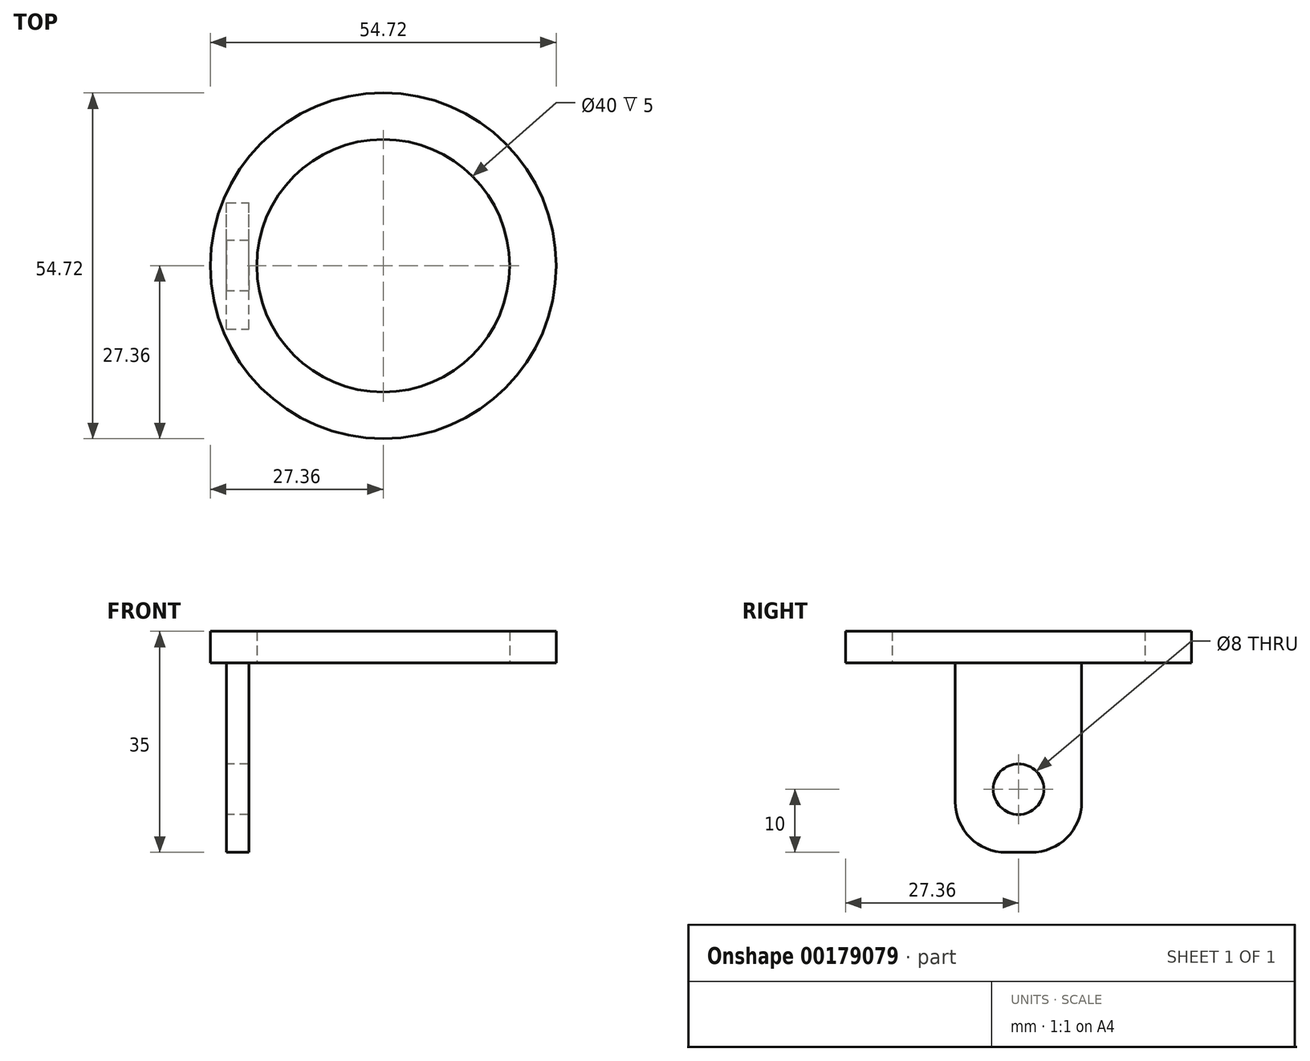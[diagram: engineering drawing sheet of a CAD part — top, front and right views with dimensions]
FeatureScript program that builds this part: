
annotation { "Feature Type Name" : "Feature", "Feature Type Description" : "" }
export const myFeature = defineFeature(function(context is Context, id is Id, definition is map)
    precondition{}
    {
        {
            var Q0;
            Q0=qCreatedBy(makeId("Top.planeOp"),FACE);
            var sketch = newSketch(context, id + "F0", { "sketchPlane" : qUnion([Q0])});
            skCircle(sketch, "E0", {"center": v(0, 0) * mm, "radius": 20 * mm});
            skCircle(sketch, "E1", {"center": v(0, 0) * mm, "radius": 27.36 * mm});
            skSolve(sketch);
        }
        {
            var Q0;
            Q0=makeQuery(id+"F0.imprint","IMPRINT",FACE,{"disambiguationData":[TD([[makeQuery(id+"F0.imprint","IMPRINT",EDGE,{"derivedFrom":sQuery(id+"F0.wireOp",EDGE,"E0")}),-1.0]])]});
            extrude(context, id + "F1", {"entities" : qUnion([Q0]), "depth" : 5 * mm});
        }
        {
            var Q0;
            Q0=makeQuery(id+"F1.opExtrude","CAP_FACE",FACE,{"disambiguationData":[OSD([sQuery(id+"F0.wireOp",EDGE,"E0"),sQuery(id+"F0.wireOp",EDGE,"E1")])],"isStart":true});
            var sketch = newSketch(context, id + "F2", { "sketchPlane" : qUnion([Q0])});
            skLineSegment(sketch, "E2.bottom", {"start": v(-24.79, 10) * mm, "end": v(-21.22, 10) * mm});
            skLineSegment(sketch, "E2.top", {"start": v(-24.79, -10) * mm, "end": v(-21.22, -10) * mm});
            skLineSegment(sketch, "E2.left", {"start": v(-24.79, 10) * mm, "end": v(-24.79, -10) * mm});
            skLineSegment(sketch, "E2.right", {"start": v(-21.22, 10) * mm, "end": v(-21.22, -10) * mm});
            skSolve(sketch);
        }
        {
            var Q0;
            Q0=makeQuery(id+"F2.imprint","IMPRINT",FACE,{"disambiguationData":[TD([[makeQuery(id+"F2.imprint","IMPRINT",EDGE,{"derivedFrom":sQuery(id+"F2.wireOp",EDGE,"E2.bottom")}),-1.0]])]});
            extrude(context, id + "F3", {"entities" : qUnion([Q0]), "operationType" : NewBodyOperationType.ADD, "depth" : 30 * mm});
        }
        {
            var Q0;
            Q0=makeQuery(id+"F3.opExtrude","SWEPT_FACE",FACE,{"disambiguationData":[OSD([sQuery(id+"F2.wireOp",EDGE,"E2.left")])]});
            var sketch = newSketch(context, id + "F4", { "sketchPlane" : qUnion([Q0])});
            skCircle(sketch, "E3", {"center": v(0, -20) * mm, "radius": 4 * mm});
            skSolve(sketch);
        }
        {
            var Q0;
            Q0=makeQuery(id+"F4.imprint","IMPRINT",FACE,{"disambiguationData":[TD([[makeQuery(id+"F4.imprint","IMPRINT",EDGE,{"derivedFrom":sQuery(id+"F4.wireOp",EDGE,"E3")}),1.0]])]});
            extrude(context, id + "F5", {"entities" : qUnion([Q0]), "operationType" : NewBodyOperationType.REMOVE, "oppositeDirection" : true, "depth" : 25 * mm});
        }
        {
            var Q0;
            Q0=makeQuery(id+"F3.opExtrude","CAP_EDGE",EDGE,{"disambiguationData":[OSD([sQuery(id+"F2.wireOp",EDGE,"E2.bottom")])],"isStart":false});
            var Q1;
            Q1=makeQuery(id+"F3.opExtrude","CAP_EDGE",EDGE,{"disambiguationData":[OSD([sQuery(id+"F2.wireOp",EDGE,"E2.top")])],"isStart":false});
            fillet(context, id + "F6", {"entities" : qUnion([Q0, Q1]), "radius" : 8 * mm, "tangentPropagation" : true, "allowEdgeOverflow" : false});
        }
    });
